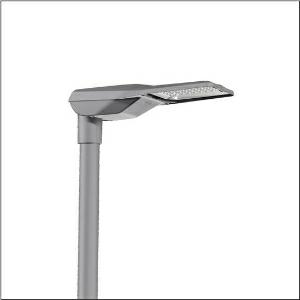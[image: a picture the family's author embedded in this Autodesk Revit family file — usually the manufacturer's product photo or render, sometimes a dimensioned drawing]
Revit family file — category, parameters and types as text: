
# Revit family: streetlight_sl_21_iq_mini___st1_0a_5xe2d21d08hb_1c5e
name_source: partatom
category: Lighting Fixtures
units: mm (PartAtom-declared; Revit-internal decimal feet)

## family parameters
Cut with Voids When Loaded = No
Host = Face
Light Source = No
Part Type = Normal
Room Calculation Point = No
Round Connector Dimension = Use Diameter
Shared = No

## types (1)
- --- (1 x LED, 7830 lm, 70.9 W, 2200K)
    Apparent Load = 71 VA
    CIE Flux Codes = 37 72 97 100 100
    Color Rendering = 70
    Color Temperature = 2200K
    Default Elevation = 1800 mm
    Description = Streetlight SL 21 iQ mini, mast luminaire, primary light control with lens, of PMMA, primary optical cover: cover, of toughened safety glass, transparent, light distribution: ST1.0a, light emission: direct distribution, primary light characteristic: asymmetric, installation type: post-top, side-entry, LED, High Power LED, rated luminous flux: 7.830lm, luminous efficacy: 110lm/W, light colour: 722, colour temperature: 2200K, control gear: iQ-Comfort, control: Auto-Match, Temp-Guard, Lumen-Switch, Night-Set, Smart-Wire, Light-Fading, Desk-Remote (wireless, voltage-free reading and setting of iQ features in the workshop via application-optimized NFC function/RFID function), optimised constant luminous flux control (CLO 2.0), pre-setting: linear dimming characteristic, mains connection: 220..240V, AC, 50/60Hz, start of lifetime: 71W, end of service life: 75W, reduction: 31W, luminaire housing, of diecast aluminium, powder-coated, Siteco® metallic grey (DB 702S), corrosivity category C5 mid according to DIN EN ISO 12944, please order mast flange separately, inclination adjustable: 0°, 5°, 10°, 15°, sealing non-destructively replaceable, multi-level sealing system, length: 628mm, width: 235mm, height: 110mm, mast flange for spigot size: 42mm (side-entry): 5XC10008XM4, 60/48mm (side-entry/post-top): 5XC10108XM2, 76/60mm (side-entry/post-top): 5XC10108XM1, mounting height: 4..8m, protection rating (complete): IP66, insulation class (complete): insulation class II (safety insulation), certification: CE, ENEC, ENEC+, VDE, impact resistance: IK10, permissible operating ambient temperature for outdoor applications: -40..+50°C, standard-compliant lighting for roads and squares, packaging unit: 1 piece

Light Distribution: ST1.0a
    Height = 110 mm
    Lamp = 1 x LED
    Lamp Light Flux = 7830 lm
    Lamp Power = 70.9 W
    Lamp count = 1
    Length = 625 mm
    Luminous efficacy = 110 lm/W
    Manufacturer = Siteco
    ModVariant = No
    Model = 5XE2D21D08HB
    Number of Poles = 1
    OnlyDefault = Yes
    Power Factor = 1
    Product Name = Streetlight SL 21 iQ mini | ST1.0a
    Product group = mast luminaire | pylon top
    ProductGroupID = 6100
    Protection Class = Protection class II
    Protection Degree = IP 66
    RLX_Detail_Level = 1
    RLX_Emergency_Light_Flux = 0 lm
    RLX_Emergency_Type = 0
    RLX_Emergency_Type_DB = No
    RlxData = <blob elided: 26245 chars, md5=114d8753>
    Socket = socket
    Standby Power = 0 W
    System Light Flux = 7830 lm
    System Power = 71 W
    Type Comments = factory setting: luminous flux: 100 % | dim-lin: 254 | 711 mA
    Type Image = l_1003519.jpg
    URL = http://relux.com
    VarID = @adj_158340
    Voltage = 0 V
    Weight = 0.00 kg
    Width = 234 mm

## geometry (parser evidence)
native form markers: Blend x4, Sweep x11
no freeform markers — native parametric forms only
